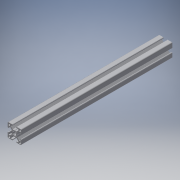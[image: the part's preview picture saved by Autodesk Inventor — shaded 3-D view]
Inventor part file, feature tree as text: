
AUTODESK INVENTOR PART (.ipt)
format: ipt  version: 2019 (Build 230136000, 136)  size: 306,688 bytes
history: native  units: in
note: dims shown in document units (in); Inventor stores cm internally (conversion verified against a paired STEP export)
features: other x3, extrude x1, sketch x1
ambient origin geometry x8: Origin, YZ Plane, XZ Plane, XY Plane, X Axis, Y Axis, Z Axis, Center Point
bodies: Solid1 (feature_tree)
feature tree (5):
  other  "Blocks"
  extrude  "Extrusion1"  [1 undecoded]
  sketch  "Sketch1"  dims[d1=0.0in]
  other  "Bosch 30x30 profile"
  other  "Bosch 30x30 profile:1"
note: 1 required parameter value undecoded (feature->parameter linkage not recoverable at this tier; creation-order binding heuristic only, values carry confidence <= 0.55)
